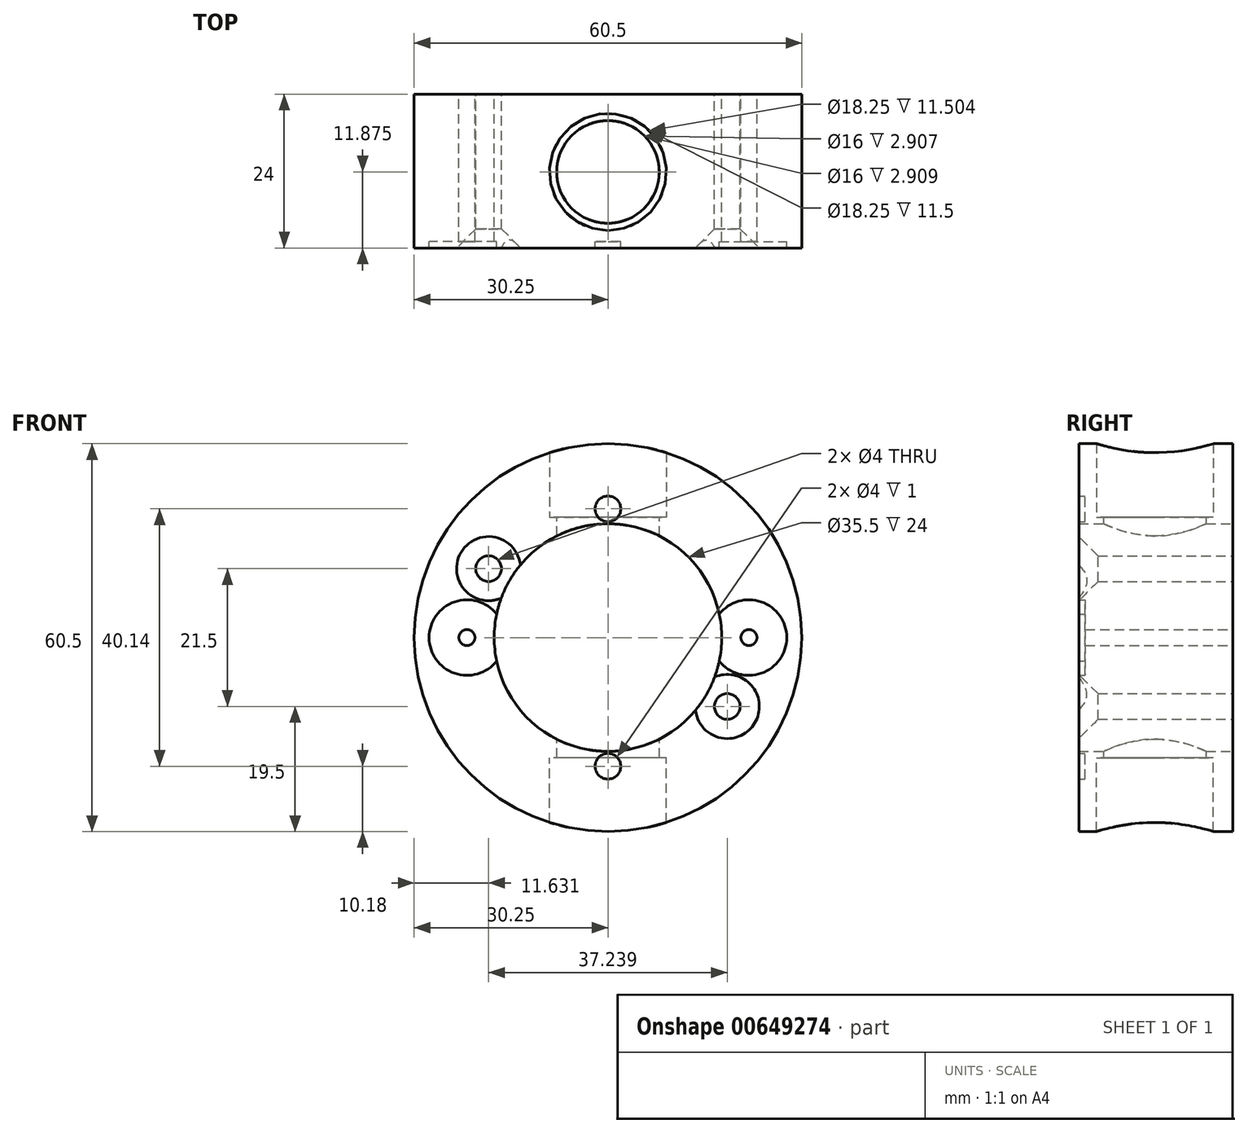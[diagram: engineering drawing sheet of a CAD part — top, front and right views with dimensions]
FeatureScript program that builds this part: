
annotation { "Feature Type Name" : "Feature", "Feature Type Description" : "" }
export const myFeature = defineFeature(function(context is Context, id is Id, definition is map)
    precondition{}
    {
        {
            var Q0;
            Q0=qCreatedBy(makeId("Front.planeOp"),FACE);
            var sketch = newSketch(context, id + "F0", { "sketchPlane" : qUnion([Q0])});
            skCircle(sketch, "E0", {"center": v(0, 0) * mm, "radius": 30.25 * mm});
            skCircle(sketch, "E1.0", {"center": v(0, 0) * mm, "radius": 17.75 * mm});
            skCircle(sketch, "E2", {"center": v(-22, 0) * mm, "radius": 1.25 * mm});
            skCircle(sketch, "E3", {"center": v(22, 0) * mm, "radius": 1.25 * mm});
            skCircle(sketch, "E4", {"center": v(-22, 0) * mm, "radius": 5.9 * mm});
            skCircle(sketch, "E5", {"center": v(22, 0) * mm, "radius": 5.9 * mm});
            skCircle(sketch, "E6", {"center": v(-18.62, 10.75) * mm, "radius": 2 * mm});
            skCircle(sketch, "E7", {"center": v(18.62, -10.75) * mm, "radius": 2 * mm});
            skLineSegment(sketch, "E8", {"start": v(0, 0) * mm, "end": v(-18.62, 10.75) * mm});
            skLineSegment(sketch, "E9", {"start": v(0, 0) * mm, "end": v(8.87, 15.37) * mm});
            skCircle(sketch, "E10", {"center": v(0, -20.07) * mm, "radius": 2 * mm});
            skCircle(sketch, "E11", {"center": v(0, 20.07) * mm, "radius": 2 * mm});
            skSolve(sketch);
        }
        {
            var Q0;
            Q0=qSketchRegion(id+"F0",true);
            extrude(context, id + "F1", {"entities" : qUnion([Q0]), "depth" : 24 * mm, "offsetDistance" : 25 * mm});
        }
        {
            var Q0;
            Q0=makeQuery(id+"F0.imprint","IMPRINT",FACE,{"disambiguationData":[TD([[makeQuery(id+"F0.imprint","IMPRINT",EDGE,{"derivedFrom":sQuery(id+"F0.wireOp",EDGE,"E2")}),-1.0]])]});
            var Q1;
            Q1=makeQuery(id+"F0.imprint","IMPRINT",FACE,{"disambiguationData":[TD([[makeQuery(id+"F0.imprint","IMPRINT",EDGE,{"derivedFrom":sQuery(id+"F0.wireOp",EDGE,"E11")}),1.0]])]});
            var Q2;
            Q2=makeQuery(id+"F0.imprint","IMPRINT",FACE,{"disambiguationData":[TD([[makeQuery(id+"F0.imprint","IMPRINT",EDGE,{"derivedFrom":sQuery(id+"F0.wireOp",EDGE,"E3")}),-1.0]])]});
            var Q3;
            Q3=makeQuery(id+"F0.imprint","IMPRINT",FACE,{"disambiguationData":[TD([[makeQuery(id+"F0.imprint","IMPRINT",EDGE,{"derivedFrom":sQuery(id+"F0.wireOp",EDGE,"E10")}),1.0]])]});
            extrude(context, id + "F2", {"entities" : qUnion([Q0, Q1, Q2, Q3]), "operationType" : NewBodyOperationType.ADD, "depth" : 23 * mm, "offsetDistance" : 25 * mm});
        }
        {
            var Q0;
            Q0=makeQuery(id+"F1.opExtrude","CAP_EDGE",EDGE,{"disambiguationData":[OSD([sQuery(id+"F0.wireOp",EDGE,"E6")])],"isStart":false});
            var Q1;
            Q1=makeQuery(id+"F1.opExtrude","CAP_EDGE",EDGE,{"disambiguationData":[OSD([sQuery(id+"F0.wireOp",EDGE,"E7")])],"isStart":false});
            chamfer(context, id + "F3", {"entities" : qUnion([Q0, Q1]), "width" : 3 * mm, "tangentPropagation" : true});
        }
        {
            var Q0;
            Q0=qCreatedBy(makeId("Top.planeOp"),FACE);
            cPlane(context, id + "F4", {"entities" : qUnion([Q0]), "cplaneType" : CPlaneType.OFFSET, "offset" : 18.75 * mm, "width" : 150 * mm, "height" : 150 * mm});
        }
        {
            var Q0;
            Q0=qCreatedBy(id+"F4.planeOp",FACE);
            var sketch = newSketch(context, id + "F5", { "sketchPlane" : qUnion([Q0])});
            skCircle(sketch, "E12", {"center": v(0, -12.12) * mm, "radius": 9.12 * mm});
            skCircle(sketch, "E13", {"center": v(0, -12.12) * mm, "radius": 8 * mm});
            skSolve(sketch);
        }
        {
            var Q0;
            Q0=qSketchRegion(id+"F5",true);
            extrude(context, id + "F6", {"entities" : qUnion([Q0]), "operationType" : NewBodyOperationType.REMOVE, "oppositeDirection" : true, "depth" : -25 * mm, "offsetDistance" : 25 * mm});
        }
        {
            var Q0;
            Q0=makeQuery(id+"F5.imprint","IMPRINT",FACE,{"disambiguationData":[TD([[makeQuery(id+"F5.imprint","IMPRINT",EDGE,{"derivedFrom":sQuery(id+"F5.wireOp",EDGE,"E13")}),1.0]])]});
            extrude(context, id + "F7", {"entities" : qUnion([Q0]), "operationType" : NewBodyOperationType.REMOVE, "oppositeDirection" : true, "depth" : 60 * mm, "offsetDistance" : 25 * mm, "hasSecondDirection" : true, "secondDirectionOppositeDirection" : true, "secondDirectionDepth" : -30 * mm});
        }
        {
            var Q0;
            Q0=makeQuery(id+"F5.imprint","IMPRINT",FACE,{"disambiguationData":[TD([[makeQuery(id+"F5.imprint","IMPRINT",EDGE,{"derivedFrom":sQuery(id+"F5.wireOp",EDGE,"E12")}),1.0]])]});
            extrude(context, id + "F8", {"entities" : qUnion([Q0]), "operationType" : NewBodyOperationType.REMOVE, "oppositeDirection" : true, "depth" : 83.2 * mm, "offsetDistance" : 25 * mm, "hasSecondDirection" : true, "secondDirectionOppositeDirection" : true, "secondDirectionDepth" : 37.5 * mm});
        }
    });
